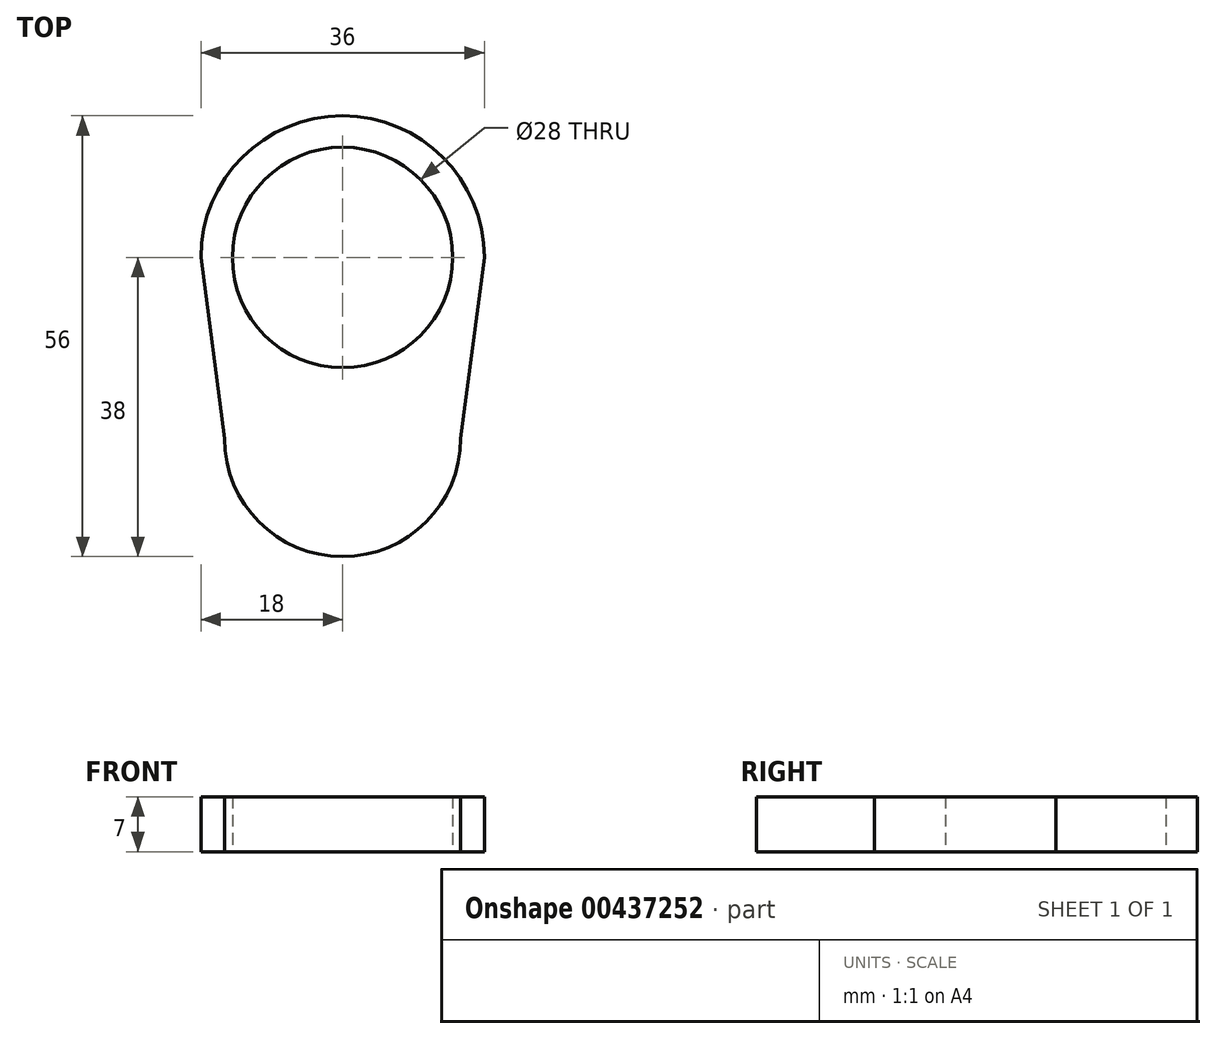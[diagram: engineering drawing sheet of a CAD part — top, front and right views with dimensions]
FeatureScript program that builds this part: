
annotation { "Feature Type Name" : "Feature", "Feature Type Description" : "" }
export const myFeature = defineFeature(function(context is Context, id is Id, definition is map)
    precondition{}
    {
        {
            var Q0;
            Q0=qCreatedBy(makeId("Top.planeOp"),FACE);
            var sketch = newSketch(context, id + "F0", { "sketchPlane" : qUnion([Q0])});
            skArc(sketch, "E0", {"start": v(18, 0) * mm, "mid": v(0, 18) * mm, "end": v(-18, 0) * mm});
            skLineSegment(sketch, "E1", {"start": v(0, 31.68) * mm, "end": v(0, -54.98) * mm, "construction": true});
            skArc(sketch, "E2", {"start": v(-15, -23) * mm, "mid": v(0, -38) * mm, "end": v(15, -23) * mm});
            skCircle(sketch, "E3", {"center": v(0, 0) * mm, "radius": 14 * mm});
            skLineSegment(sketch, "E4", {"start": v(-43.8, -23) * mm, "end": v(38.84, -23) * mm, "construction": true});
            skPoint(sketch, "E5", {"position": v(-15, -23) * mm});
            skPoint(sketch, "E6", {"position": v(15, -23) * mm});
            skPoint(sketch, "E7", {"position": v(-18, 0) * mm});
            skPoint(sketch, "E8", {"position": v(18, 0) * mm});
            skLineSegment(sketch, "E9", {"start": v(-15, -23) * mm, "end": v(-18, 0) * mm});
            skLineSegment(sketch, "E10", {"start": v(18, 0) * mm, "end": v(15, -23) * mm});
            skSolve(sketch);
        }
        {
            var Q0;
            Q0=makeQuery(id+"F0.imprint","IMPRINT",FACE,{"disambiguationData":[TD([[makeQuery(id+"F0.imprint","IMPRINT",EDGE,{"derivedFrom":sQuery(id+"F0.wireOp",EDGE,"E0")}),1.0]])]});
            extrude(context, id + "F1", {"entities" : qUnion([Q0]), "depth" : 7 * mm});
        }
    });
